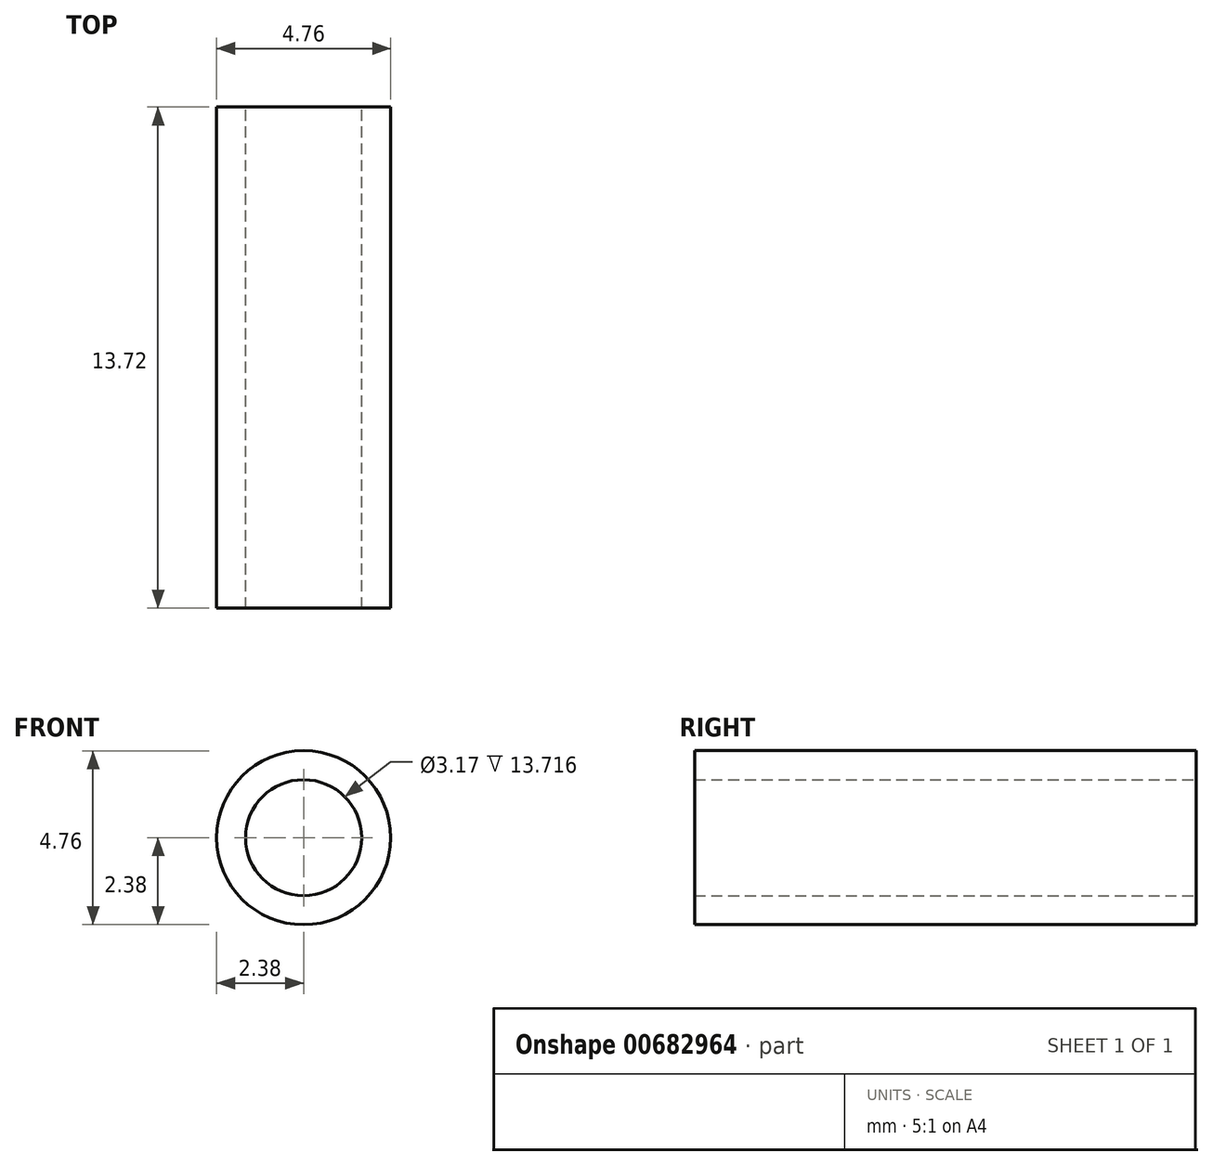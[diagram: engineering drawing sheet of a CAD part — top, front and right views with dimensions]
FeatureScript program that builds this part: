
annotation { "Feature Type Name" : "Feature", "Feature Type Description" : "" }
export const myFeature = defineFeature(function(context is Context, id is Id, definition is map)
    precondition{}
    {
        {
            var Q0;
            Q0=qCreatedBy(makeId("Front.planeOp"),FACE);
            var sketch = newSketch(context, id + "F0", { "sketchPlane" : qUnion([Q0])});
            skCircle(sketch, "E0", {"center": v(0, 0) * mm, "radius": 2.38 * mm});
            skCircle(sketch, "E1", {"center": v(0, 0) * mm, "radius": 1.59 * mm});
            skSolve(sketch);
        }
        {
            var Q0;
            Q0=makeQuery(id+"F0.imprint","IMPRINT",FACE,{"disambiguationData":[TD([[makeQuery(id+"F0.imprint","IMPRINT",EDGE,{"derivedFrom":sQuery(id+"F0.wireOp",EDGE,"E0")}),1.0]])]});
            extrude(context, id + "F1", {"entities" : qUnion([Q0]), "depth" : 13.72 * mm, "offsetDistance" : 25.4 * mm});
        }
    });
